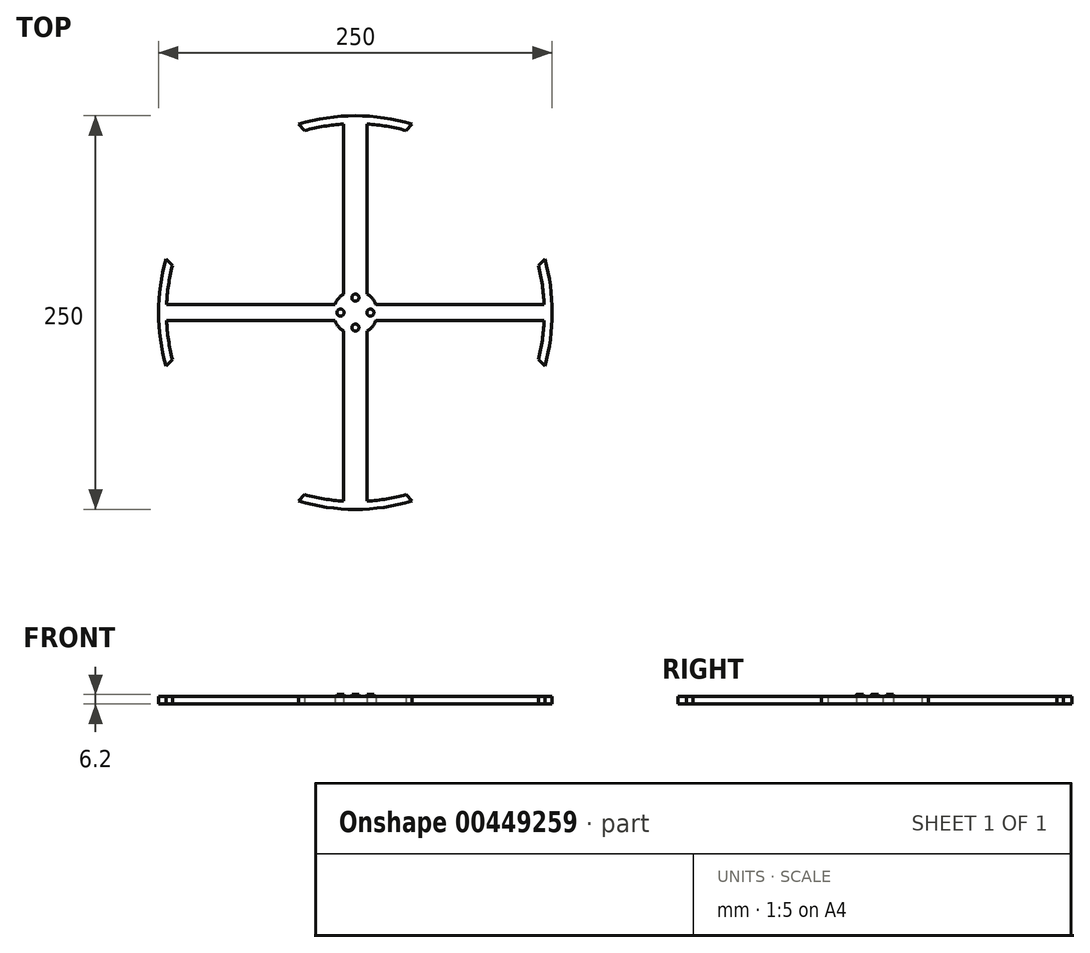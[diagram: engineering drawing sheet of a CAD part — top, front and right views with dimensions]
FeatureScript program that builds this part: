
annotation { "Feature Type Name" : "Feature", "Feature Type Description" : "" }
export const myFeature = defineFeature(function(context is Context, id is Id, definition is map)
    precondition{}
    {
        {
            var Q0;
            Q0=qCreatedBy(makeId("Top.planeOp"),FACE);
            var sketch = newSketch(context, id + "F0", { "sketchPlane" : qUnion([Q0])});
            skArc(sketch, "E0", {"start": v(-119.9, -5) * mm, "mid": v(-118.72, -17.46) * mm, "end": v(-116.26, -29.73) * mm});
            skArc(sketch, "E1", {"start": v(-36.12, -119.67) * mm, "mid": v(0, -125) * mm, "end": v(36.12, -119.67) * mm});
            skLineSegment(sketch, "E2.left", {"start": v(-7.5, 119.77) * mm, "end": v(-7.5, 5) * mm});
            skLineSegment(sketch, "E2.right", {"start": v(7.5, 119.77) * mm, "end": v(7.5, 5) * mm});
            skLineSegment(sketch, "E3.bottom", {"start": v(119.9, 5) * mm, "end": v(7.5, 5) * mm});
            skLineSegment(sketch, "E3.top", {"start": v(119.9, -5) * mm, "end": v(7.5, -5) * mm});
            skLineSegment(sketch, "E4.trimOffspring", {"start": v(-7.5, 5) * mm, "end": v(-119.9, 5) * mm});
            skLineSegment(sketch, "E5.trimOffspring", {"start": v(-7.5, -5) * mm, "end": v(-7.5, -119.77) * mm});
            skLineSegment(sketch, "E6.trimOffspring", {"start": v(-7.5, -5) * mm, "end": v(-119.9, -5) * mm});
            skLineSegment(sketch, "E7.trimOffspring", {"start": v(7.5, -5) * mm, "end": v(7.5, -119.77) * mm});
            skArc(sketch, "E8.trimOffspring", {"start": v(119.9, 5) * mm, "mid": v(118.72, 17.46) * mm, "end": v(116.26, 29.73) * mm});
            skArc(sketch, "E9.trimOffspring", {"start": v(-7.5, 119.77) * mm, "mid": v(-19.93, 118.33) * mm, "end": v(-32.15, 115.61) * mm});
            skArc(sketch, "E10.trimOffspring", {"start": v(7.5, -119.77) * mm, "mid": v(19.93, -118.33) * mm, "end": v(32.15, -115.61) * mm});
            skLineSegment(sketch, "E11", {"start": v(7.5, -119.77) * mm, "end": v(119.9, -5) * mm, "construction": true});
            skLineSegment(sketch, "E12", {"start": v(119.9, 5) * mm, "end": v(7.5, 119.77) * mm, "construction": true});
            skLineSegment(sketch, "E13", {"start": v(-7.5, 119.77) * mm, "end": v(-119.9, 5) * mm, "construction": true});
            skLineSegment(sketch, "E14", {"start": v(-119.9, -5) * mm, "end": v(-7.5, -119.77) * mm, "construction": true});
            skLineSegment(sketch, "E15", {"start": v(7.5, 5) * mm, "end": v(63.7, 62.38) * mm, "construction": true});
            skLineSegment(sketch, "E16", {"start": v(-7.5, 5) * mm, "end": v(-63.7, 62.38) * mm, "construction": true});
            skLineSegment(sketch, "E17", {"start": v(-7.5, -5) * mm, "end": v(-63.7, -62.38) * mm, "construction": true});
            skLineSegment(sketch, "E18", {"start": v(36.12, 119.67) * mm, "end": v(32.15, 115.61) * mm});
            skLineSegment(sketch, "E19", {"start": v(120.32, 33.88) * mm, "end": v(116.26, 29.73) * mm});
            skLineSegment(sketch, "E20", {"start": v(-32.15, -115.61) * mm, "end": v(-36.12, -119.67) * mm});
            skLineSegment(sketch, "E21", {"start": v(-116.26, -29.73) * mm, "end": v(-120.32, -33.88) * mm});
            skArc(sketch, "E22.trimOffspring", {"start": v(-32.15, -115.61) * mm, "mid": v(-19.93, -118.33) * mm, "end": v(-7.5, -119.77) * mm});
            skArc(sketch, "E23.trimOffspring", {"start": v(36.12, 119.67) * mm, "mid": v(0, 125) * mm, "end": v(-36.12, 119.67) * mm});
            skArc(sketch, "E24.trimOffspring", {"start": v(32.15, 115.61) * mm, "mid": v(19.93, 118.33) * mm, "end": v(7.5, 119.77) * mm});
            skLineSegment(sketch, "E25", {"start": v(-120.32, 33.88) * mm, "end": v(-116.26, 29.73) * mm});
            skLineSegment(sketch, "E26", {"start": v(116.26, -29.73) * mm, "end": v(120.32, -33.88) * mm});
            skLineSegment(sketch, "E27", {"start": v(32.15, -115.61) * mm, "end": v(36.12, -119.67) * mm});
            skArc(sketch, "E28.trimOffspring", {"start": v(-120.32, 33.88) * mm, "mid": v(-125, 0) * mm, "end": v(-120.32, -33.88) * mm});
            skArc(sketch, "E29.trimOffspring", {"start": v(-116.26, 29.73) * mm, "mid": v(-118.72, 17.46) * mm, "end": v(-119.9, 5) * mm});
            skArc(sketch, "E30.trimOffspring", {"start": v(116.26, -29.73) * mm, "mid": v(118.72, -17.46) * mm, "end": v(119.9, -5) * mm});
            skPoint(sketch, "E31.end.orphan", {"position": v(63.7, -62.38) * mm});
            skArc(sketch, "E32.trimOffspring", {"start": v(120.32, -33.88) * mm, "mid": v(125, 0) * mm, "end": v(120.32, 33.88) * mm});
            skLineSegment(sketch, "E33", {"start": v(-36.12, 119.67) * mm, "end": v(-32.15, 115.61) * mm});
            skSolve(sketch);
        }
        {
            var Q0;
            Q0=makeQuery(id+"F0.imprint","IMPRINT",FACE,{"disambiguationData":[TD([[makeQuery(id+"F0.imprint","IMPRINT",EDGE,{"derivedFrom":sQuery(id+"F0.wireOp",EDGE,"E0")}),-1.0]])]});
            extrude(context, id + "F1", {"entities" : qUnion([Q0]), "depth" : 5 * mm});
        }
        {
            var Q0;
            Q0=makeQuery(id+"F1.opExtrude","CAP_FACE",FACE,{"disambiguationData":[OSD([sQuery(id+"F0.wireOp",EDGE,"E0"),sQuery(id+"F0.wireOp",EDGE,"E1"),sQuery(id+"F0.wireOp",EDGE,"E2.left"),sQuery(id+"F0.wireOp",EDGE,"E2.right"),sQuery(id+"F0.wireOp",EDGE,"E3.bottom"),sQuery(id+"F0.wireOp",EDGE,"E3.top"),sQuery(id+"F0.wireOp",EDGE,"E4.trimOffspring"),sQuery(id+"F0.wireOp",EDGE,"E5.trimOffspring"),sQuery(id+"F0.wireOp",EDGE,"E6.trimOffspring"),sQuery(id+"F0.wireOp",EDGE,"E7.trimOffspring"),sQuery(id+"F0.wireOp",EDGE,"E8.trimOffspring"),sQuery(id+"F0.wireOp",EDGE,"E9.trimOffspring"),sQuery(id+"F0.wireOp",EDGE,"E10.trimOffspring"),sQuery(id+"F0.wireOp",EDGE,"E18"),sQuery(id+"F0.wireOp",EDGE,"E19"),sQuery(id+"F0.wireOp",EDGE,"E20"),sQuery(id+"F0.wireOp",EDGE,"E21"),sQuery(id+"F0.wireOp",EDGE,"E22.trimOffspring"),sQuery(id+"F0.wireOp",EDGE,"E23.trimOffspring"),sQuery(id+"F0.wireOp",EDGE,"E24.trimOffspring"),sQuery(id+"F0.wireOp",EDGE,"E25"),sQuery(id+"F0.wireOp",EDGE,"E26"),sQuery(id+"F0.wireOp",EDGE,"E27"),sQuery(id+"F0.wireOp",EDGE,"E28.trimOffspring"),sQuery(id+"F0.wireOp",EDGE,"E29.trimOffspring"),sQuery(id+"F0.wireOp",EDGE,"E30.trimOffspring"),sQuery(id+"F0.wireOp",EDGE,"E32.trimOffspring"),sQuery(id+"F0.wireOp",EDGE,"E33")])],"isStart":true});
            var sketch = newSketch(context, id + "F2", { "sketchPlane" : qUnion([Q0])});
            skCircle(sketch, "E34", {"center": v(0, 0) * mm, "radius": 14 * mm});
            skSolve(sketch);
        }
        {
            var Q0;
            {var subQ0=sQuery(id+"F2.wireOp",EDGE,"E34");var subQ1=makeQuery(id+"F1.opExtrude","CAP_EDGE",EDGE,{"disambiguationData":[OSD([sQuery(id+"F0.wireOp",EDGE,"E7.trimOffspring")])],"isStart":true});var subQ2=makeQuery(id+"F2.imprint","INTERSECT",VERTEX,{"derivedFrom":[subQ1,subQ0]});Q0=makeQuery(id+"F2.imprint","IMPRINT",FACE,{"disambiguationData":[TD([[makeQuery(id+"F2.imprint","IMPRINT",EDGE,{"disambiguationData":[TD([[subQ2,1.0]])],"derivedFrom":subQ0}),1.0]])]});}
            var Q1;
            {var subQ0=sQuery(id+"F2.wireOp",EDGE,"E34");var subQ1=makeQuery(id+"F1.opExtrude","CAP_EDGE",EDGE,{"disambiguationData":[OSD([sQuery(id+"F0.wireOp",EDGE,"E2.right")])],"isStart":true});var subQ2=makeQuery(id+"F2.imprint","INTERSECT",VERTEX,{"derivedFrom":[subQ1,subQ0]});Q1=makeQuery(id+"F2.imprint","IMPRINT",FACE,{"disambiguationData":[TD([[makeQuery(id+"F2.imprint","IMPRINT",EDGE,{"disambiguationData":[TD([[subQ2,-1.0]])],"derivedFrom":subQ0}),1.0]])]});}
            var Q2;
            {var subQ0=sQuery(id+"F2.wireOp",EDGE,"E34");var subQ1=makeQuery(id+"F1.opExtrude","CAP_EDGE",EDGE,{"disambiguationData":[OSD([sQuery(id+"F0.wireOp",EDGE,"E4.trimOffspring")])],"isStart":true});var subQ2=makeQuery(id+"F2.imprint","INTERSECT",VERTEX,{"derivedFrom":[subQ1,subQ0]});Q2=makeQuery(id+"F2.imprint","IMPRINT",FACE,{"disambiguationData":[TD([[makeQuery(id+"F2.imprint","IMPRINT",EDGE,{"disambiguationData":[TD([[subQ2,-1.0]])],"derivedFrom":subQ0}),1.0]])]});}
            var Q3;
            {var subQ0=sQuery(id+"F2.wireOp",EDGE,"E34");var subQ1=makeQuery(id+"F1.opExtrude","CAP_EDGE",EDGE,{"disambiguationData":[OSD([sQuery(id+"F0.wireOp",EDGE,"E5.trimOffspring")])],"isStart":true});var subQ2=makeQuery(id+"F2.imprint","INTERSECT",VERTEX,{"derivedFrom":[subQ1,subQ0]});Q3=makeQuery(id+"F2.imprint","IMPRINT",FACE,{"disambiguationData":[TD([[makeQuery(id+"F2.imprint","IMPRINT",EDGE,{"disambiguationData":[TD([[subQ2,-1.0]])],"derivedFrom":subQ0}),1.0]])]});}
            extrude(context, id + "F3", {"entities" : qUnion([Q0, Q1, Q2, Q3]), "operationType" : NewBodyOperationType.ADD, "oppositeDirection" : true, "depth" : 5 * mm});
        }
        {
            var Q0;
            {var subQ0=sQuery(id+"F2.wireOp",EDGE,"E34");var subQ1=sQuery(id+"F0.wireOp",EDGE,"E3.bottom");var subQ2=sQuery(id+"F0.wireOp",EDGE,"E2.right");var subQ3=sQuery(id+"F0.wireOp",EDGE,"E4.trimOffspring");var subQ4=sQuery(id+"F0.wireOp",EDGE,"E2.left");var subQ5=sQuery(id+"F0.wireOp",EDGE,"E6.trimOffspring");var subQ6=sQuery(id+"F0.wireOp",EDGE,"E5.trimOffspring");var subQ7=sQuery(id+"F0.wireOp",EDGE,"E7.trimOffspring");var subQ8=sQuery(id+"F0.wireOp",EDGE,"E3.top");Q0=makeQuery(id+"F3.boolean.opBoolean","MERGE",FACE,{"derivedFrom":[makeQuery(id+"F1.opExtrude","CAP_FACE",FACE,{"disambiguationData":[OSD([sQuery(id+"F0.wireOp",EDGE,"E0"),sQuery(id+"F0.wireOp",EDGE,"E1"),subQ4,subQ2,subQ1,subQ8,subQ3,subQ6,subQ5,subQ7,sQuery(id+"F0.wireOp",EDGE,"E8.trimOffspring"),sQuery(id+"F0.wireOp",EDGE,"E9.trimOffspring"),sQuery(id+"F0.wireOp",EDGE,"E10.trimOffspring"),sQuery(id+"F0.wireOp",EDGE,"E18"),sQuery(id+"F0.wireOp",EDGE,"E19"),sQuery(id+"F0.wireOp",EDGE,"E20"),sQuery(id+"F0.wireOp",EDGE,"E21"),sQuery(id+"F0.wireOp",EDGE,"E22.trimOffspring"),sQuery(id+"F0.wireOp",EDGE,"E23.trimOffspring"),sQuery(id+"F0.wireOp",EDGE,"E24.trimOffspring"),sQuery(id+"F0.wireOp",EDGE,"E25"),sQuery(id+"F0.wireOp",EDGE,"E26"),sQuery(id+"F0.wireOp",EDGE,"E27"),sQuery(id+"F0.wireOp",EDGE,"E28.trimOffspring"),sQuery(id+"F0.wireOp",EDGE,"E29.trimOffspring"),sQuery(id+"F0.wireOp",EDGE,"E30.trimOffspring"),sQuery(id+"F0.wireOp",EDGE,"E32.trimOffspring"),sQuery(id+"F0.wireOp",EDGE,"E33")])],"isStart":false}),makeQuery(id+"F3.opExtrude","CAP_FACE",FACE,{"disambiguationData":[OSD([subQ8,subQ7,subQ0])],"isStart":false}),makeQuery(id+"F3.opExtrude","CAP_FACE",FACE,{"disambiguationData":[OSD([subQ6,subQ5,subQ0])],"isStart":false}),makeQuery(id+"F3.opExtrude","CAP_FACE",FACE,{"disambiguationData":[OSD([subQ4,subQ3,subQ0])],"isStart":false}),makeQuery(id+"F3.opExtrude","CAP_FACE",FACE,{"disambiguationData":[OSD([subQ2,subQ1,subQ0])],"isStart":false})]});}
            var sketch = newSketch(context, id + "F4", { "sketchPlane" : qUnion([Q0])});
            skCircle(sketch, "E35", {"center": v(0, 9.5) * mm, "radius": 2.25 * mm});
            skCircle(sketch, "E36.1.0", {"center": v(-9.5, 0) * mm, "radius": 2.25 * mm});
            skCircle(sketch, "E36.2.0", {"center": v(0, -9.5) * mm, "radius": 2.25 * mm});
            skPoint(sketch, "E36.center", {"position": v(0, 0) * mm});
            skCircle(sketch, "E37.1.3.0", {"center": v(9.5, 0) * mm, "radius": 2.25 * mm});
            skSolve(sketch);
        }
        {
            var Q0;
            Q0=makeQuery(id+"F4.imprint","IMPRINT",FACE,{"disambiguationData":[TD([[makeQuery(id+"F4.imprint","IMPRINT",EDGE,{"derivedFrom":sQuery(id+"F4.wireOp",EDGE,"E35")}),1.0]])]});
            var Q1;
            Q1=makeQuery(id+"F4.imprint","IMPRINT",FACE,{"disambiguationData":[TD([[makeQuery(id+"F4.imprint","IMPRINT",EDGE,{"derivedFrom":sQuery(id+"F4.wireOp",EDGE,"E36.1.0")}),1.0]])]});
            var Q2;
            Q2=makeQuery(id+"F4.imprint","IMPRINT",FACE,{"disambiguationData":[TD([[makeQuery(id+"F4.imprint","IMPRINT",EDGE,{"derivedFrom":sQuery(id+"F4.wireOp",EDGE,"E36.2.0")}),1.0]])]});
            var Q3;
            Q3=makeQuery(id+"F4.imprint","IMPRINT",FACE,{"disambiguationData":[TD([[makeQuery(id+"F4.imprint","IMPRINT",EDGE,{"derivedFrom":sQuery(id+"F4.wireOp",EDGE,"E37.1.3.0")}),1.0]])]});
            extrude(context, id + "F5", {"entities" : qUnion([Q0, Q1, Q2, Q3]), "operationType" : NewBodyOperationType.ADD, "depth" : 1.2 * mm});
        }
    });
